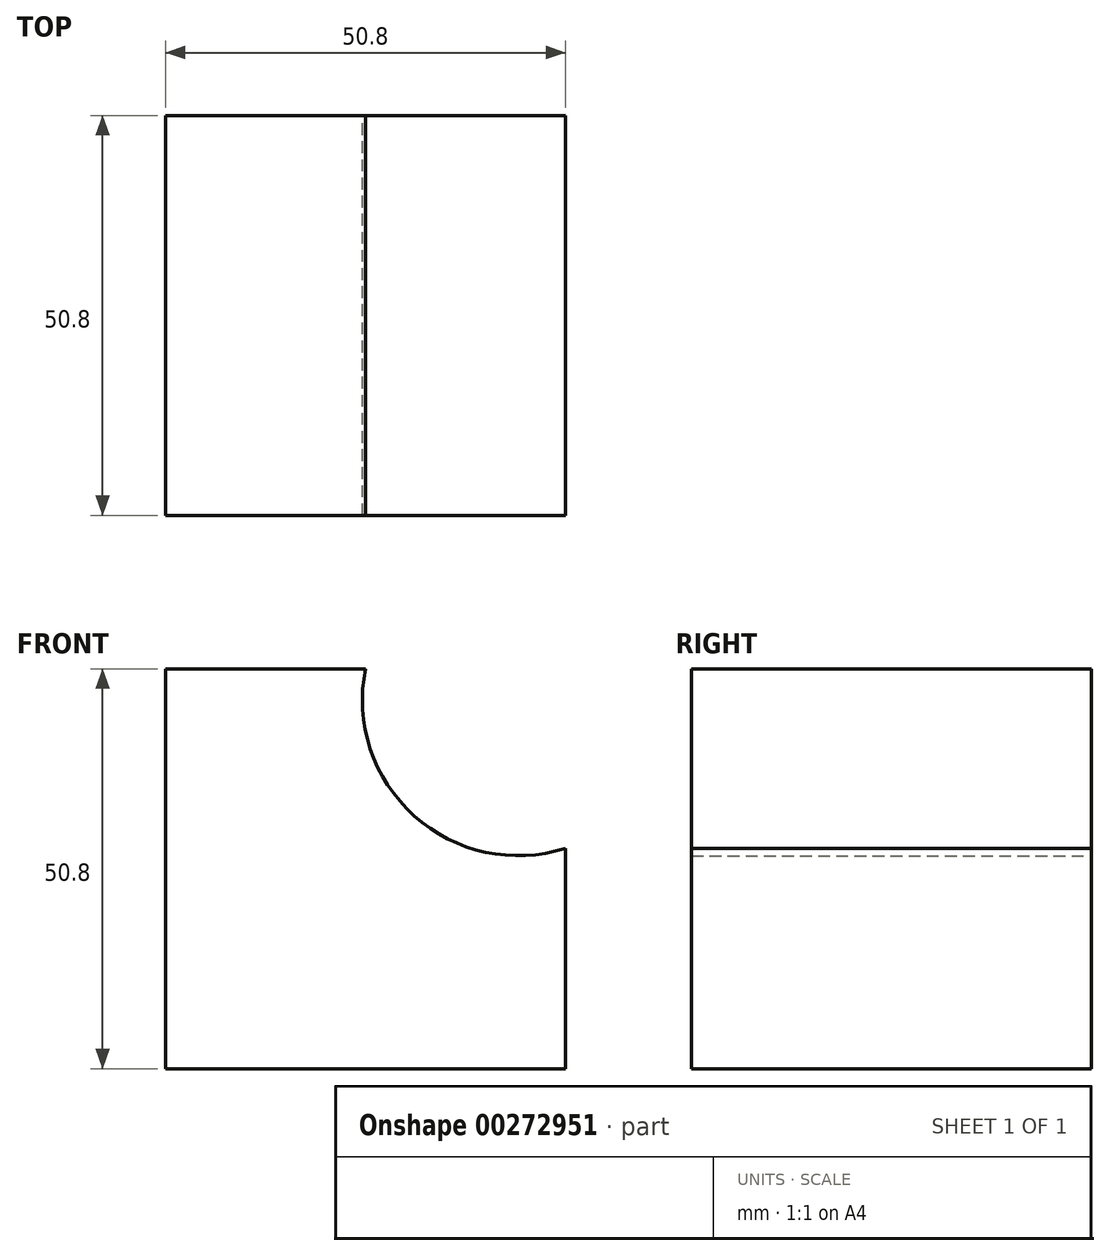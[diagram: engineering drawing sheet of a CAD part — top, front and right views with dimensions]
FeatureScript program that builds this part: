
annotation { "Feature Type Name" : "Feature", "Feature Type Description" : "" }
export const myFeature = defineFeature(function(context is Context, id is Id, definition is map)
    precondition{}
    {
        {
            var Q0;
            Q0=qCreatedBy(makeId("Front.planeOp"),FACE);
            var sketch = newSketch(context, id + "F0", { "sketchPlane" : qUnion([Q0])});
            skLineSegment(sketch, "E0", {"start": v(0, 0) * mm, "end": v(-50.8, 0) * mm});
            skLineSegment(sketch, "E1", {"start": v(-50.8, 0) * mm, "end": v(-50.8, 50.8) * mm});
            skLineSegment(sketch, "E2", {"start": v(-50.8, 50.8) * mm, "end": v(0, 50.8) * mm});
            skLineSegment(sketch, "E3", {"start": v(0, 50.8) * mm, "end": v(0, 0) * mm});
            skLineSegment(sketch, "E4", {"start": v(0, 50.8) * mm, "end": v(0, 81.55) * mm});
            skLineSegment(sketch, "E5", {"start": v(0, 81.55) * mm, "end": v(0, 20.05) * mm});
            skArc(sketch, "E6", {"start": v(-25.4, 50.8) * mm, "mid": v(-19.23, 32.12) * mm, "end": v(0, 27.99) * mm});
            skSolve(sketch);
        }
        {
            var Q0;
            Q0=makeQuery(id+"F0.imprint","IMPRINT",FACE,{"disambiguationData":[TD([[makeQuery(id+"F0.imprint","IMPRINT",EDGE,{"derivedFrom":sQuery(id+"F0.wireOp",EDGE,"E0")}),-1.0]])]});
            extrude(context, id + "F1", {"entities" : qUnion([Q0]), "depth" : 50.8 * mm});
        }
    });
